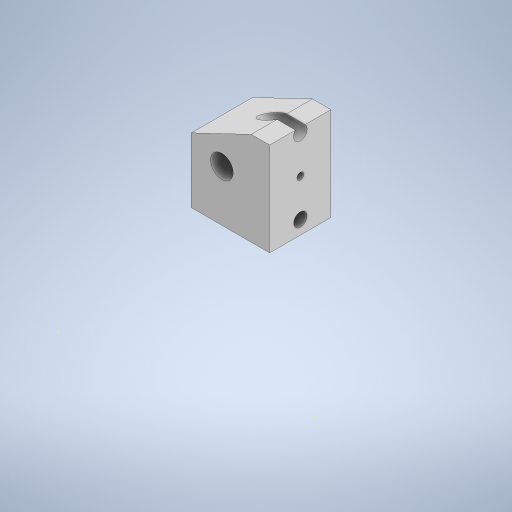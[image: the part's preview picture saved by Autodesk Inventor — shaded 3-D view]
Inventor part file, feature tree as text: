
AUTODESK INVENTOR PART (.ipt)
format: ipt  version: 2024 (Build 280153000, 153)  size: 559,104 bytes
history: native  units: mm
features: sketch x26, extrude x21, move_body x4, chamfer x3, plane x3, split x3, boolean_combine x2, other x1, fillet x1, imported_body x1
ambient origin geometry x8: Origin, YZ Plane, XZ Plane, XY Plane, X Axis, Y Axis, Z Axis, Center Point
bodies: Solid1 (feature_tree), Solid2 (feature_tree), Solid3 (feature_tree), Solid4 (feature_tree), Solid5 (feature_tree), Solid6 (feature_tree), Solid7 (feature_tree), Solid8 (feature_tree)
feature tree (65):
  other  "Repaired Geometry1"
  extrude  "Extrusion1"  Depth=16.0mm
  sketch  "Sketch2"  dims[d2=15.0mm d3=0.0mm d4=10.0mm]
  extrude  "Extrusion2"  Depth=10.0mm
  chamfer  "Chamfer1"  Distance=21.25mm
  extrude  "Extrusion3"  Depth=10.0mm TaperAngle=0.0deg
  extrude  "Extrusion4"  Depth=11.5mm TaperAngle=0.0deg
  extrude  "Extrusion5"  Depth=1.0mm TaperAngle=0.0deg
  chamfer  "Chamfer2"  Distance=6.0mm Angle=45.0deg
  sketch  "Sketch6"  dims[d14=7.0mm d15=11.5mm d16=0.0mm]
  extrude  "Extrusion6"  Depth=9.0mm
  extrude  "Extrusion7"  Depth=11.5mm TaperAngle=0.0deg
  chamfer  "Chamfer3"  Distance=11.5mm Angle=45.0deg
  sketch  "Sketch9"  dims[d26=3.3mm d27=45.25mm d28=0.0mm d29=11.5mm d30=5.5mm d31=45.0deg]
  extrude  "Extrusion8"  Depth=65.75mm TaperAngle=0.0deg
  extrude  "Extrusion9"  Depth=9.0mm TaperAngle=0.0deg
  extrude  "Extrusion10"  Depth=13.0mm TaperAngle=0.0deg
  sketch  "Sketch13"  dims[d43=24.0mm d44=21.0mm d45=0.0mm]
  extrude  "Extrusion11"  Depth=21.0mm TaperAngle=0.0deg
  extrude  "Extrusion12"  TaperAngle=0.0deg  [1 undecoded]
  extrude  "Extrusion13"  Depth=6.0mm TaperAngle=0.0deg
  plane  "Work Plane1"
  split  "Split1"
  move_body  "Move Body1"
  extrude  "Extrusion14"  Depth=0.5mm TaperAngle=0.0deg
  move_body  "Move Body2"
  fillet  "Fillet1"  Radius=10.0mm
  extrude  "Extrusion15"  Depth=10.0mm TaperAngle=0.0deg
  sketch  "Sketch19"  dims[d71=29.5mm d72=0.0mm d73=13.75mm]
  sketch  "Sketch20"  dims[d74=26.0mm d75=0.0mm d76=-5.0mm d77=0.0mm d78=0.0mm]
  extrude  "Extrusion16"  Depth=1.0mm
  extrude  "Extrusion18"  Depth=29.5mm
  extrude  "Extrusion19"  TaperAngle=0.0deg  [1 undecoded]
  sketch  "Sketch23"  dims[d83=1.0mm d84=1.0mm d85=0.0mm]
  sketch  "Sketch24"
  extrude  "Extrusion20"  TaperAngle=0.0deg  [1 undecoded]
  plane  "Work Plane2"
  boolean_combine  "Combine1"
  split  "Split2"
  extrude  "Extrusion21"  Depth=1.0mm TaperAngle=0.0deg
  move_body  "Move Body3"
  boolean_combine  "Combine2"
  plane  "Work Plane3"
  split  "Split3"
  move_body  "Move Body4"
  extrude  "Extrusion22"  [1 undecoded]
  sketch  "Sketch1"  dims[d0=36.0mm d1=16.0mm]
  sketch  "Sketch3"  dims[d5=10.0mm]
  sketch  "Sketch4"  dims[d6=3.3mm d7=21.25mm d8=0.0mm]
  sketch  "Sketch5"  dims[d9=10.0mm d10=5.5mm d11=45.0deg d12=10.0mm d13=0.0mm]
  sketch  "Sketch7"  dims[d17=3.3mm d18=1.0mm d19=0.0mm d20=6.0mm d21=11.5mm d22=45.0deg]
  sketch  "Sketch8"  dims[d23=15.0mm d24=0.0mm d25=9.0mm]
  sketch  "Sketch10"  dims[d32=2.0mm d33=65.75mm d34=0.0mm]
  sketch  "Sketch11"  dims[d35=0.5mm d36=0.0mm d37=9.0mm d38=0.0mm]
  sketch  "Sketch12"  dims[d39=0.5mm d40=0.0mm d41=13.0mm d42=0.0mm]
  sketch  "Sketch14"  dims[d46=12.25mm d47=-12.0mm d48=0.0mm d49=0.0mm]
  sketch  "Sketch15"  dims[d50=30.0mm d51=0.0mm d52=6.0mm d53=0.0mm d54=0.0mm d55=4.0mm]
  sketch  "Sketch16"  dims[d56=0.5mm d57=0.0mm d58=0.5mm d59=0.0mm d64=10.0mm d65=0.0mm]
  sketch  "Sketch17"  dims[d66=3.0mm d67=10.0mm d68=0.0mm]
  sketch  "Sketch18"  dims[d69=1.0mm d70=31.0mm]
  sketch  "Sketch22"  dims[d79=0.0mm d80=0.0mm d81=0.0mm d82=-30.0mm]
  sketch  "Sketch25"
  sketch  "Sketch26"
  imported_body  "Base1"
  sketch  "Sketch27"
note: 4 required parameter values undecoded (feature->parameter linkage not recoverable at this tier; creation-order binding heuristic only, values carry confidence <= 0.55)
